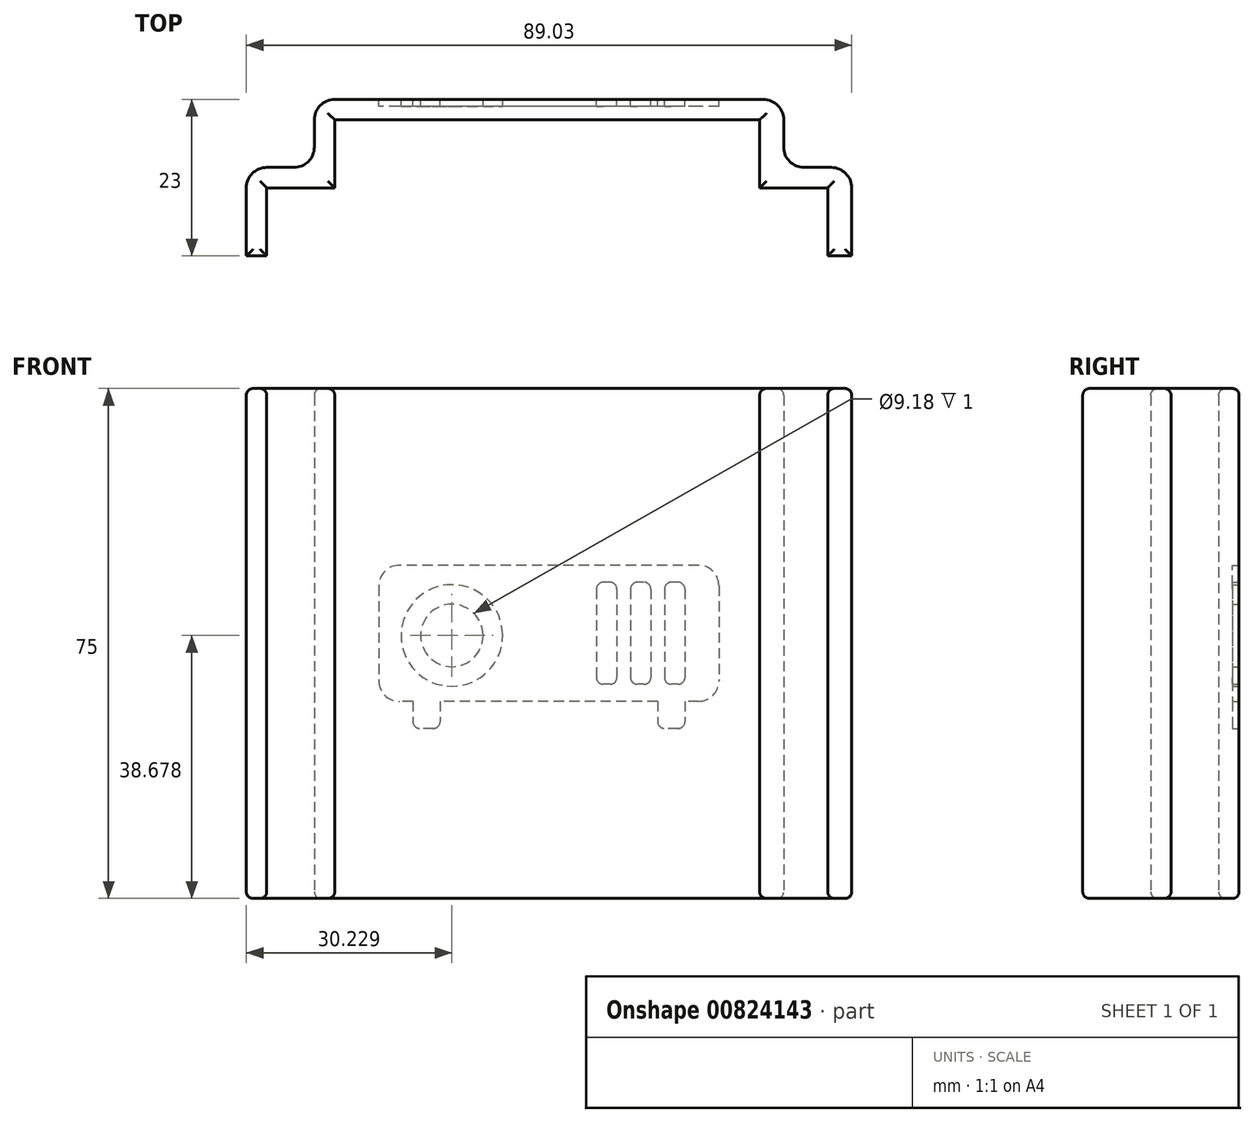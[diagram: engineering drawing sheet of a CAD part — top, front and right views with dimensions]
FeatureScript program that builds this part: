
annotation { "Feature Type Name" : "Feature", "Feature Type Description" : "" }
export const myFeature = defineFeature(function(context is Context, id is Id, definition is map)
    precondition{}
    {
        {
            var Q0;
            Q0=qCreatedBy(makeId("Top.planeOp"),FACE);
            var sketch = newSketch(context, id + "F0", { "sketchPlane" : qUnion([Q0])});
            skLineSegment(sketch, "E0", {"start": v(0, 0) * mm, "end": v(0, 10) * mm});
            skLineSegment(sketch, "E1", {"start": v(0, 10) * mm, "end": v(10, 10) * mm});
            skLineSegment(sketch, "E2", {"start": v(10, 10) * mm, "end": v(10, 20) * mm});
            skLineSegment(sketch, "E3", {"start": v(10, 20) * mm, "end": v(72.5, 20) * mm});
            skLineSegment(sketch, "E4", {"start": v(72.5, 20) * mm, "end": v(72.5, 10) * mm});
            skLineSegment(sketch, "E5", {"start": v(72.5, 10) * mm, "end": v(82.5, 10) * mm});
            skLineSegment(sketch, "E6", {"start": v(82.5, 10) * mm, "end": v(82.5, 0) * mm});
            skLineSegment(sketch, "E7", {"start": v(82.5, 0) * mm, "end": v(86.03, 0) * mm});
            skLineSegment(sketch, "E8", {"start": v(86.03, 0) * mm, "end": v(86.03, 13) * mm});
            skLineSegment(sketch, "E9", {"start": v(86.03, 13) * mm, "end": v(76.03, 13) * mm});
            skLineSegment(sketch, "E10", {"start": v(76.03, 13) * mm, "end": v(76.03, 23) * mm});
            skLineSegment(sketch, "E11", {"start": v(76.03, 23) * mm, "end": v(7, 23) * mm});
            skLineSegment(sketch, "E12", {"start": v(7, 23) * mm, "end": v(7, 13) * mm});
            skLineSegment(sketch, "E13", {"start": v(7, 13) * mm, "end": v(-3, 13) * mm});
            skLineSegment(sketch, "E14", {"start": v(-3, 13) * mm, "end": v(-3, 0) * mm});
            skLineSegment(sketch, "E15", {"start": v(-3, 0) * mm, "end": v(0, 0) * mm});
            skSolve(sketch);
        }
        {
            var Q0;
            Q0=makeQuery(id+"F0.imprint","IMPRINT",FACE,{"disambiguationData":[TD([[makeQuery(id+"F0.imprint","IMPRINT",EDGE,{"derivedFrom":sQuery(id+"F0.wireOp",EDGE,"E0")}),1.0]])]});
            extrude(context, id + "F1", {"entities" : qUnion([Q0]), "depth" : 75 * mm, "offsetDistance" : 25 * mm});
        }
        {
            var Q0;
            Q0=makeQuery(id+"F1.opExtrude","SWEPT_EDGE",EDGE,{"disambiguationData":[OSD([sQuery(id+"F0.wireOp",EDGE,"E13"),sQuery(id+"F0.wireOp",EDGE,"E14")])]});
            var Q1;
            Q1=makeQuery(id+"F1.opExtrude","SWEPT_EDGE",EDGE,{"disambiguationData":[OSD([sQuery(id+"F0.wireOp",EDGE,"E12"),sQuery(id+"F0.wireOp",EDGE,"E13")])]});
            var Q2;
            Q2=makeQuery(id+"F1.opExtrude","SWEPT_EDGE",EDGE,{"disambiguationData":[OSD([sQuery(id+"F0.wireOp",EDGE,"E11"),sQuery(id+"F0.wireOp",EDGE,"E12")])]});
            var Q3;
            Q3=makeQuery(id+"F1.opExtrude","SWEPT_EDGE",EDGE,{"disambiguationData":[OSD([sQuery(id+"F0.wireOp",EDGE,"E10"),sQuery(id+"F0.wireOp",EDGE,"E11")])]});
            var Q4;
            Q4=makeQuery(id+"F1.opExtrude","SWEPT_EDGE",EDGE,{"disambiguationData":[OSD([sQuery(id+"F0.wireOp",EDGE,"E9"),sQuery(id+"F0.wireOp",EDGE,"E10")])]});
            var Q5;
            Q5=makeQuery(id+"F1.opExtrude","SWEPT_EDGE",EDGE,{"disambiguationData":[OSD([sQuery(id+"F0.wireOp",EDGE,"E8"),sQuery(id+"F0.wireOp",EDGE,"E9")])]});
            fillet(context, id + "F2", {"entities" : qUnion([Q0, Q1, Q2, Q3, Q4, Q5]), "radius" : 3 * mm, "tangentPropagation" : true, "allowEdgeOverflow" : false});
        }
        {
            var Q0;
            Q0=makeQuery(id+"F1.opExtrude","CAP_FACE",FACE,{"disambiguationData":[OSD([sQuery(id+"F0.wireOp",EDGE,"E0"),sQuery(id+"F0.wireOp",EDGE,"E1"),sQuery(id+"F0.wireOp",EDGE,"E2"),sQuery(id+"F0.wireOp",EDGE,"E3"),sQuery(id+"F0.wireOp",EDGE,"E4"),sQuery(id+"F0.wireOp",EDGE,"E5"),sQuery(id+"F0.wireOp",EDGE,"E6"),sQuery(id+"F0.wireOp",EDGE,"E7"),sQuery(id+"F0.wireOp",EDGE,"E8"),sQuery(id+"F0.wireOp",EDGE,"E9"),sQuery(id+"F0.wireOp",EDGE,"E10"),sQuery(id+"F0.wireOp",EDGE,"E11"),sQuery(id+"F0.wireOp",EDGE,"E12"),sQuery(id+"F0.wireOp",EDGE,"E13"),sQuery(id+"F0.wireOp",EDGE,"E14"),sQuery(id+"F0.wireOp",EDGE,"E15")])],"isStart":false});
            var Q1;
            Q1=makeQuery(id+"F1.opExtrude","CAP_FACE",FACE,{"disambiguationData":[OSD([sQuery(id+"F0.wireOp",EDGE,"E0"),sQuery(id+"F0.wireOp",EDGE,"E1"),sQuery(id+"F0.wireOp",EDGE,"E2"),sQuery(id+"F0.wireOp",EDGE,"E3"),sQuery(id+"F0.wireOp",EDGE,"E4"),sQuery(id+"F0.wireOp",EDGE,"E5"),sQuery(id+"F0.wireOp",EDGE,"E6"),sQuery(id+"F0.wireOp",EDGE,"E7"),sQuery(id+"F0.wireOp",EDGE,"E8"),sQuery(id+"F0.wireOp",EDGE,"E9"),sQuery(id+"F0.wireOp",EDGE,"E10"),sQuery(id+"F0.wireOp",EDGE,"E11"),sQuery(id+"F0.wireOp",EDGE,"E12"),sQuery(id+"F0.wireOp",EDGE,"E13"),sQuery(id+"F0.wireOp",EDGE,"E14"),sQuery(id+"F0.wireOp",EDGE,"E15")])],"isStart":true});
            fillet(context, id + "F3", {"entities" : qUnion([Q0, Q1]), "radius" : 1 * mm, "tangentPropagation" : true, "allowEdgeOverflow" : false});
        }
        {
            var Q0;
            Q0=makeQuery(id+"F1.opExtrude","SWEPT_FACE",FACE,{"disambiguationData":[OSD([sQuery(id+"F0.wireOp",EDGE,"E11")])]});
            var sketch = newSketch(context, id + "F4", { "sketchPlane" : qUnion([Q0])});
            skLineSegment(sketch, "E16.bottom", {"start": v(-63.5, 49) * mm, "end": v(-19.5, 49) * mm});
            skLineSegment(sketch, "E16.top", {"start": v(-63.5, 29) * mm, "end": v(-61.5, 29) * mm});
            skLineSegment(sketch, "E16.left", {"start": v(-66.5, 46) * mm, "end": v(-66.5, 32) * mm});
            skLineSegment(sketch, "E16.right", {"start": v(-16.5, 46) * mm, "end": v(-16.5, 32) * mm});
            skLineSegment(sketch, "E17.bottom", {"start": v(-60.5, 46.5) * mm, "end": v(-59.5, 46.5) * mm});
            skLineSegment(sketch, "E17.top", {"start": v(-60.5, 31.5) * mm, "end": v(-59.5, 31.5) * mm});
            skLineSegment(sketch, "E17.left", {"start": v(-61.5, 45.5) * mm, "end": v(-61.5, 32.5) * mm});
            skLineSegment(sketch, "E17.right", {"start": v(-58.5, 45.5) * mm, "end": v(-58.5, 32.5) * mm});
            skCircle(sketch, "E18", {"center": v(-27.23, 38.68) * mm, "radius": 7.47 * mm});
            skCircle(sketch, "E19", {"center": v(-27.23, 38.68) * mm, "radius": 4.6 * mm});
            skLineSegment(sketch, "E20.top", {"start": v(-60.5, 25) * mm, "end": v(-58.5, 25) * mm});
            skLineSegment(sketch, "E20.left", {"start": v(-61.5, 29) * mm, "end": v(-61.5, 26) * mm});
            skLineSegment(sketch, "E20.right", {"start": v(-57.5, 29) * mm, "end": v(-57.5, 26) * mm});
            skLineSegment(sketch, "E21.top", {"start": v(-24.5, 25) * mm, "end": v(-22.5, 25) * mm});
            skLineSegment(sketch, "E21.left", {"start": v(-25.5, 29) * mm, "end": v(-25.5, 26) * mm});
            skLineSegment(sketch, "E21.right", {"start": v(-21.5, 29) * mm, "end": v(-21.5, 26) * mm});
            skLineSegment(sketch, "E22.1.0.0", {"start": v(-55.5, 46.5) * mm, "end": v(-54.5, 46.5) * mm});
            skLineSegment(sketch, "E22.1.0.1", {"start": v(-53.5, 45.5) * mm, "end": v(-53.5, 32.5) * mm});
            skLineSegment(sketch, "E22.1.0.2", {"start": v(-56.5, 45.5) * mm, "end": v(-56.5, 32.5) * mm});
            skLineSegment(sketch, "E22.1.0.3", {"start": v(-55.5, 31.5) * mm, "end": v(-54.5, 31.5) * mm});
            skLineSegment(sketch, "E22.2.0.0", {"start": v(-50.5, 46.5) * mm, "end": v(-49.5, 46.5) * mm});
            skLineSegment(sketch, "E22.2.0.1", {"start": v(-48.5, 45.5) * mm, "end": v(-48.5, 32.5) * mm});
            skLineSegment(sketch, "E22.2.0.2", {"start": v(-51.5, 45.5) * mm, "end": v(-51.5, 32.5) * mm});
            skLineSegment(sketch, "E22.2.0.3", {"start": v(-50.5, 31.5) * mm, "end": v(-49.5, 31.5) * mm});
            skLineSegment(sketch, "E22.direction1", {"start": v(-61.5, 31.5) * mm, "end": v(-56.5, 31.5) * mm, "construction": true});
            skLineSegment(sketch, "E23.trimOffspring", {"start": v(-21.5, 29) * mm, "end": v(-19.5, 29) * mm});
            skLineSegment(sketch, "E24.trimOffspring", {"start": v(-57.5, 29) * mm, "end": v(-25.5, 29) * mm});
            skPoint(sketch, "E25.visualSharp", {"position": v(-66.5, 49) * mm});
            skArc(sketch, "E25.filletArc", {"start": v(-63.5, 49) * mm, "mid": v(-65.62, 48.12) * mm, "end": v(-66.5, 46) * mm});
            skPoint(sketch, "E26.visualSharp", {"position": v(-16.5, 49) * mm});
            skArc(sketch, "E26.filletArc", {"start": v(-16.5, 46) * mm, "mid": v(-17.38, 48.12) * mm, "end": v(-19.5, 49) * mm});
            skPoint(sketch, "E27.visualSharp", {"position": v(-16.5, 29) * mm});
            skArc(sketch, "E27.filletArc", {"start": v(-19.5, 29) * mm, "mid": v(-17.38, 29.88) * mm, "end": v(-16.5, 32) * mm});
            skPoint(sketch, "E28.visualSharp", {"position": v(-66.5, 29) * mm});
            skArc(sketch, "E28.filletArc", {"start": v(-66.5, 32) * mm, "mid": v(-65.62, 29.88) * mm, "end": v(-63.5, 29) * mm});
            skPoint(sketch, "E29.visualSharp", {"position": v(-61.5, 25) * mm});
            skArc(sketch, "E29.filletArc", {"start": v(-61.5, 26) * mm, "mid": v(-61.2, 25.3) * mm, "end": v(-60.5, 25) * mm});
            skPoint(sketch, "E30.visualSharp", {"position": v(-57.5, 25) * mm});
            skArc(sketch, "E30.filletArc", {"start": v(-58.5, 25) * mm, "mid": v(-57.8, 25.3) * mm, "end": v(-57.5, 26) * mm});
            skPoint(sketch, "E31.visualSharp", {"position": v(-25.5, 25) * mm});
            skArc(sketch, "E31.filletArc", {"start": v(-25.5, 26) * mm, "mid": v(-25.2, 25.3) * mm, "end": v(-24.5, 25) * mm});
            skPoint(sketch, "E32.visualSharp", {"position": v(-21.5, 25) * mm});
            skArc(sketch, "E32.filletArc", {"start": v(-22.5, 25) * mm, "mid": v(-21.8, 25.3) * mm, "end": v(-21.5, 26) * mm});
            skPoint(sketch, "E33.visualSharp", {"position": v(-61.5, 46.5) * mm});
            skArc(sketch, "E33.filletArc", {"start": v(-60.5, 46.5) * mm, "mid": v(-61.2, 46.2) * mm, "end": v(-61.5, 45.5) * mm});
            skPoint(sketch, "E34.visualSharp", {"position": v(-58.5, 46.5) * mm});
            skArc(sketch, "E34.filletArc", {"start": v(-58.5, 45.5) * mm, "mid": v(-58.8, 46.2) * mm, "end": v(-59.5, 46.5) * mm});
            skPoint(sketch, "E35.visualSharp", {"position": v(-58.5, 31.5) * mm});
            skArc(sketch, "E35.filletArc", {"start": v(-59.5, 31.5) * mm, "mid": v(-58.8, 31.8) * mm, "end": v(-58.5, 32.5) * mm});
            skPoint(sketch, "E36.visualSharp", {"position": v(-61.5, 31.5) * mm});
            skArc(sketch, "E36.filletArc", {"start": v(-61.5, 32.5) * mm, "mid": v(-61.2, 31.8) * mm, "end": v(-60.5, 31.5) * mm});
            skPoint(sketch, "E37.visualSharp", {"position": v(-56.5, 46.5) * mm});
            skArc(sketch, "E37.filletArc", {"start": v(-55.5, 46.5) * mm, "mid": v(-56.2, 46.2) * mm, "end": v(-56.5, 45.5) * mm});
            skPoint(sketch, "E38.visualSharp", {"position": v(-56.5, 31.5) * mm});
            skArc(sketch, "E38.filletArc", {"start": v(-56.5, 32.5) * mm, "mid": v(-56.2, 31.8) * mm, "end": v(-55.5, 31.5) * mm});
            skPoint(sketch, "E39.visualSharp", {"position": v(-53.5, 31.5) * mm});
            skArc(sketch, "E39.filletArc", {"start": v(-54.5, 31.5) * mm, "mid": v(-53.8, 31.8) * mm, "end": v(-53.5, 32.5) * mm});
            skPoint(sketch, "E40.visualSharp", {"position": v(-51.5, 46.5) * mm});
            skArc(sketch, "E40.filletArc", {"start": v(-50.5, 46.5) * mm, "mid": v(-51.2, 46.2) * mm, "end": v(-51.5, 45.5) * mm});
            skPoint(sketch, "E41.visualSharp", {"position": v(-48.5, 46.5) * mm});
            skArc(sketch, "E41.filletArc", {"start": v(-48.5, 45.5) * mm, "mid": v(-48.8, 46.2) * mm, "end": v(-49.5, 46.5) * mm});
            skPoint(sketch, "E42.visualSharp", {"position": v(-48.5, 31.5) * mm});
            skArc(sketch, "E42.filletArc", {"start": v(-49.5, 31.5) * mm, "mid": v(-48.8, 31.8) * mm, "end": v(-48.5, 32.5) * mm});
            skPoint(sketch, "E43.visualSharp", {"position": v(-53.5, 46.5) * mm});
            skArc(sketch, "E43.filletArc", {"start": v(-53.5, 45.5) * mm, "mid": v(-53.8, 46.2) * mm, "end": v(-54.5, 46.5) * mm});
            skPoint(sketch, "E44.visualSharp", {"position": v(-51.5, 31.5) * mm});
            skArc(sketch, "E44.filletArc", {"start": v(-51.5, 32.5) * mm, "mid": v(-51.2, 31.8) * mm, "end": v(-50.5, 31.5) * mm});
            skSolve(sketch);
        }
        {
            var Q0;
            Q0=makeQuery(id+"F4.imprint","IMPRINT",FACE,{"disambiguationData":[TD([[makeQuery(id+"F4.imprint","IMPRINT",EDGE,{"derivedFrom":sQuery(id+"F4.wireOp",EDGE,"E16.bottom")}),-1.0]])]});
            var Q1;
            Q1=makeQuery(id+"F4.imprint","IMPRINT",FACE,{"disambiguationData":[TD([[makeQuery(id+"F4.imprint","IMPRINT",EDGE,{"derivedFrom":sQuery(id+"F4.wireOp",EDGE,"E19")}),1.0]])]});
            extrude(context, id + "F5", {"entities" : qUnion([Q0, Q1]), "operationType" : NewBodyOperationType.REMOVE, "oppositeDirection" : true, "depth" : 1 * mm, "offsetDistance" : 25 * mm});
        }
    });
